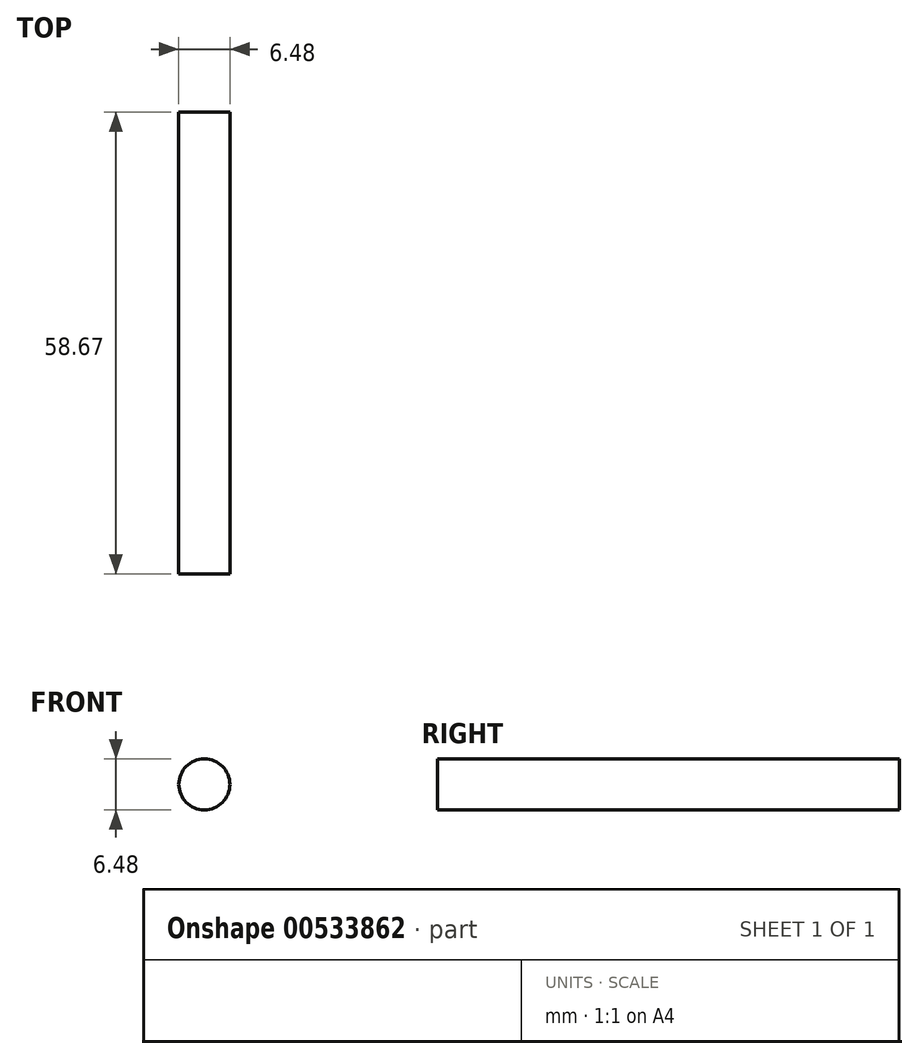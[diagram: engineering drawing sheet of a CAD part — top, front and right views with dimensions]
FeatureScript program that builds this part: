
annotation { "Feature Type Name" : "Feature", "Feature Type Description" : "" }
export const myFeature = defineFeature(function(context is Context, id is Id, definition is map)
    precondition{}
    {
        {
            var Q0;
            Q0=qCreatedBy(makeId("Front.planeOp"),FACE);
            var sketch = newSketch(context, id + "F0", { "sketchPlane" : qUnion([Q0])});
            skCircle(sketch, "E0", {"center": v(0, 0) * mm, "radius": 3.24 * mm});
            skSolve(sketch);
        }
        {
            var Q0;
            Q0=makeQuery(id+"F0.imprint","IMPRINT",FACE,{"disambiguationData":[TD([[makeQuery(id+"F0.imprint","IMPRINT",EDGE,{"derivedFrom":sQuery(id+"F0.wireOp",EDGE,"E0")}),1.0]])]});
            extrude(context, id + "F1", {"entities" : qUnion([Q0]), "depth" : 58.67 * mm, "offsetDistance" : 25.4 * mm});
        }
    });
